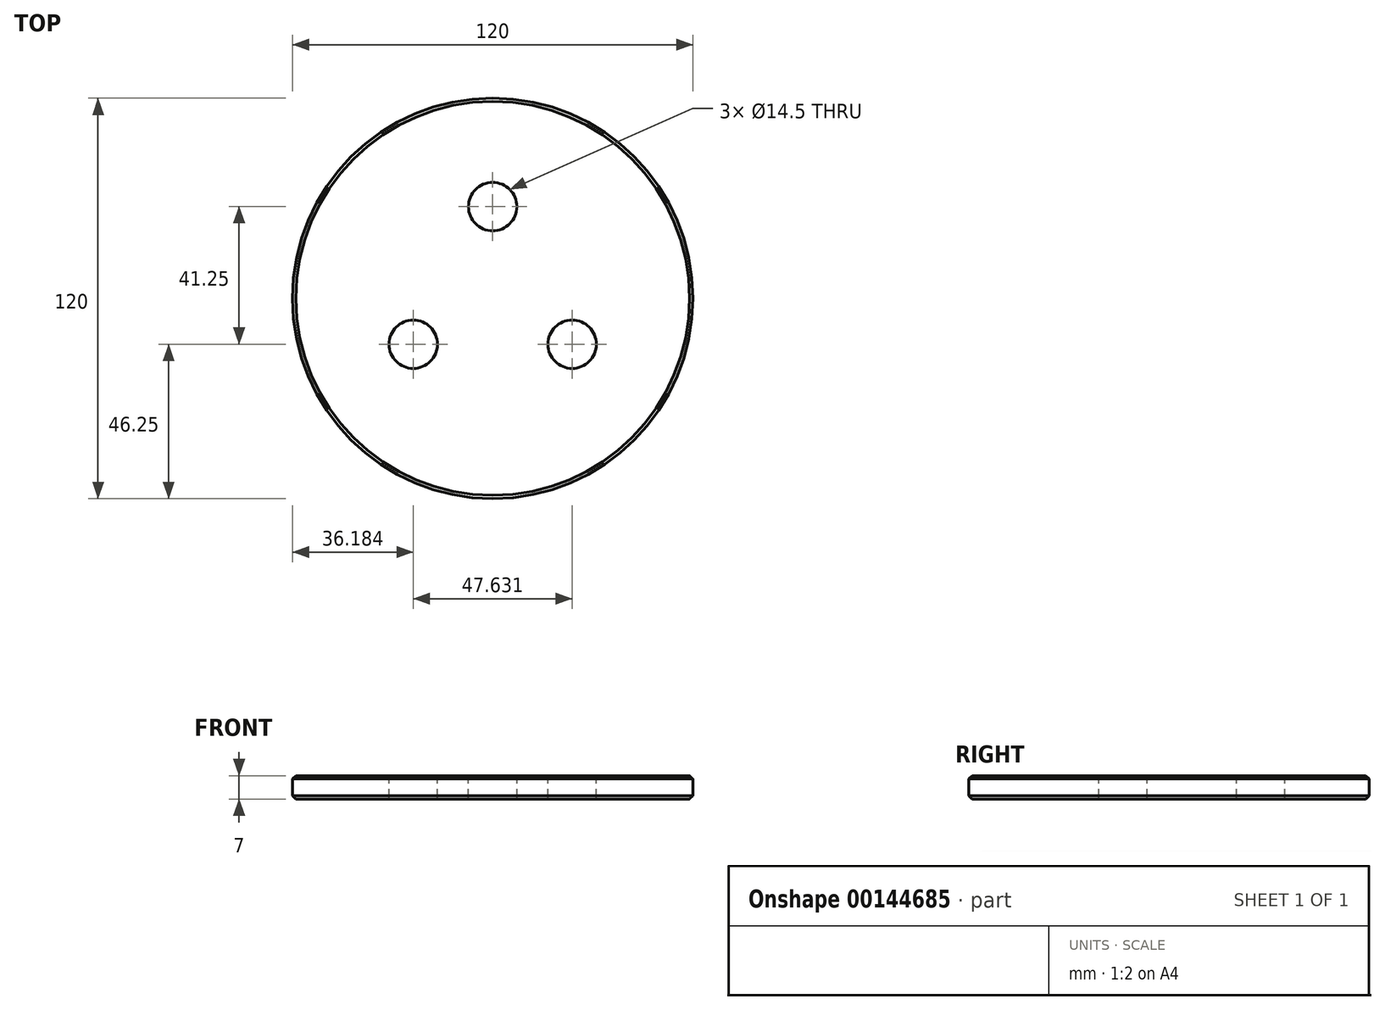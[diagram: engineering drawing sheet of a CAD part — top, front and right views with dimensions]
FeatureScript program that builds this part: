
annotation { "Feature Type Name" : "Feature", "Feature Type Description" : "" }
export const myFeature = defineFeature(function(context is Context, id is Id, definition is map)
    precondition{}
    {
        {
            var Q0;
            Q0=qCreatedBy(makeId("Top.planeOp"),FACE);
            var sketch = newSketch(context, id + "F0", { "sketchPlane" : qUnion([Q0])});
            skCircle(sketch, "E0", {"center": v(0, 0) * mm, "radius": 60 * mm});
            skSolve(sketch);
        }
        {
            var Q0;
            Q0 = qSketchRegion(id + "F0", true);
            extrude(context, id + "F1", {"entities" : qUnion([Q0]), "depth" : 7 * mm});
        }
        {
            var Q0;
            Q0=makeQuery(id+"F1.opExtrude","CAP_EDGE",EDGE,{"disambiguationData":[OSD([sQuery(id+"F0.wireOp",EDGE,"E0")])],"isStart":false});
            var Q1;
            Q1=makeQuery(id+"F1.opExtrude","CAP_EDGE",EDGE,{"disambiguationData":[OSD([sQuery(id+"F0.wireOp",EDGE,"E0")])],"isStart":true});
            chamfer(context, id + "F2", {"entities" : qUnion([Q0, Q1]), "width" : 1 * mm, "tangentPropagation" : true});
        }
        {
            var Q0;
            Q0=makeQuery(id+"F1.opExtrude","CAP_FACE",FACE,{"disambiguationData":[OSD([sQuery(id+"F0.wireOp",EDGE,"E0")])],"isStart":false});
            var sketch = newSketch(context, id + "F3", { "sketchPlane" : qUnion([Q0])});
            skCircle(sketch, "E1", {"center": v(0, 0) * mm, "radius": 27.5 * mm, "construction": true});
            skLineSegment(sketch, "E2", {"start": v(0, 0) * mm, "end": v(0, 27.5) * mm, "construction": true});
            skPoint(sketch, "E3", {"position": v(0, 27.5) * mm});
            skPoint(sketch, "E4.1.0", {"position": v(-23.82, -13.75) * mm});
            skPoint(sketch, "E4.2.0", {"position": v(23.82, -13.75) * mm});
            skSolve(sketch);
        }
        {
            var Q0;
            Q0=sQuery(id+"F3.wireOp",VERTEX,"E3");
            var Q1;
            Q1=sQuery(id+"F3.wireOp",VERTEX,"E4.2.0");
            var Q2;
            Q2=sQuery(id+"F3.wireOp",VERTEX,"E4.1.0");
            var Q3;
            Q3=makeQuery(id+"F1.opExtrude","SWEPT_BODY",BODY,{"disambiguationData":[OSD([sQuery(id+"F0.wireOp",EDGE,"E0")])]});
            hole(context, id + "F4", {"style" : HoleStyle.SIMPLE, "endStyle" : HoleEndStyle.THROUGH, "standardTappedOrClearance" : lookupTablePath({ "standard" : "ISO", "size" : "14.5", "type" : "Drilled" }), "standardBlindInLast" : lookupTablePath({ "standard" : "ISO", "size" : "14.5", "type" : "Drilled" }), "holeDiameter" : 14.5 * mm, "startFromSketch" : true, "locations" : qUnion([Q0, Q1, Q2]), "scope" : qUnion([Q3]), "isTappedThrough" : true});
        }
    });
